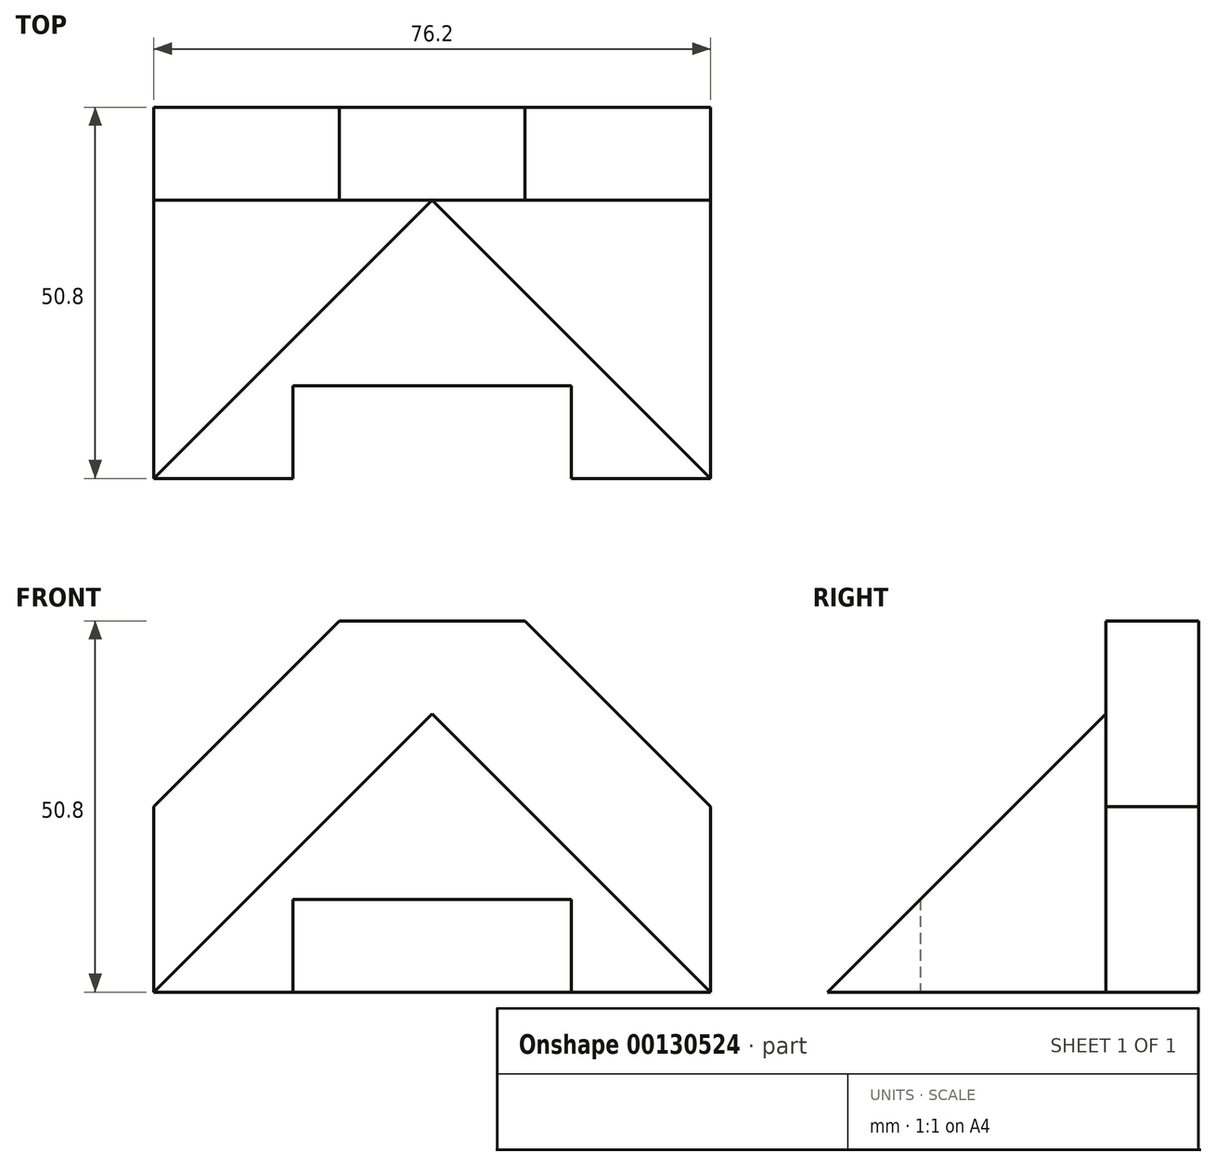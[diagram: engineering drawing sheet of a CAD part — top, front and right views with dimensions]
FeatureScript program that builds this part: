
annotation { "Feature Type Name" : "Feature", "Feature Type Description" : "" }
export const myFeature = defineFeature(function(context is Context, id is Id, definition is map)
    precondition{}
    {
        {
            var Q0;
            Q0=qCreatedBy(makeId("Front.planeOp"),FACE);
            var sketch = newSketch(context, id + "F0", { "sketchPlane" : qUnion([Q0])});
            skLineSegment(sketch, "E0", {"start": v(0, 0) * mm, "end": v(-76.2, 0) * mm});
            skLineSegment(sketch, "E1", {"start": v(-76.2, 0) * mm, "end": v(-76.2, 25.4) * mm});
            skLineSegment(sketch, "E2", {"start": v(-76.2, 25.4) * mm, "end": v(-50.8, 50.8) * mm});
            skLineSegment(sketch, "E3", {"start": v(-50.8, 50.8) * mm, "end": v(-25.4, 50.8) * mm});
            skLineSegment(sketch, "E4", {"start": v(-25.4, 50.8) * mm, "end": v(0, 25.4) * mm});
            skLineSegment(sketch, "E5", {"start": v(0, 25.4) * mm, "end": v(0, 0) * mm});
            skLineSegment(sketch, "E6", {"start": v(-76.2, 0) * mm, "end": v(-38.1, 38.1) * mm});
            skPoint(sketch, "E6.endSnap0", {"position": v(-38.1, 0) * mm});
            skLineSegment(sketch, "E7", {"start": v(-38.1, 38.1) * mm, "end": v(0, 0) * mm});
            skLineSegment(sketch, "E8", {"start": v(-57.15, 0) * mm, "end": v(-57.15, 12.7) * mm});
            skLineSegment(sketch, "E9", {"start": v(-57.15, 12.7) * mm, "end": v(-19.05, 12.7) * mm});
            skLineSegment(sketch, "E10", {"start": v(-19.05, 12.7) * mm, "end": v(-19.05, 0) * mm});
            skLineSegment(sketch, "E11", {"start": v(-19.05, 0) * mm, "end": v(-57.15, 0) * mm});
            skLineSegment(sketch, "E12", {"start": v(-38.1, 38.1) * mm, "end": v(-63.5, 38.1) * mm});
            skLineSegment(sketch, "E13", {"start": v(-63.5, 38.1) * mm, "end": v(-76.2, 25.4) * mm});
            skLineSegment(sketch, "E14", {"start": v(-38.1, 38.1) * mm, "end": v(-12.7, 38.1) * mm});
            skLineSegment(sketch, "E15", {"start": v(-12.7, 38.1) * mm, "end": v(0, 25.4) * mm});
            skLineSegment(sketch, "E16", {"start": v(0, 0) * mm, "end": v(-38.1, 38.1) * mm});
            skSolve(sketch);
        }
        {
            var Q0;
            Q0 = qSketchRegion(id + "F0", true);
            extrude(context, id + "F1", {"entities" : qUnion([Q0]), "endBound" : BoundingType.SYMMETRIC, "depth" : 50.8 * mm});
        }
        {
            var Q0;
            Q0=qCreatedBy(makeId("Right.planeOp"),FACE);
            var sketch = newSketch(context, id + "F2", { "sketchPlane" : qUnion([Q0])});
            skLineSegment(sketch, "E17", {"start": v(12.7, 50.8) * mm, "end": v(12.7, 38.1) * mm});
            skLineSegment(sketch, "E18", {"start": v(12.7, 38.1) * mm, "end": v(-25.4, 0) * mm});
            skLineSegment(sketch, "E19", {"start": v(-25.4, 0) * mm, "end": v(-25.4, 50.8) * mm});
            skLineSegment(sketch, "E20", {"start": v(-25.4, 50.8) * mm, "end": v(12.7, 50.8) * mm});
            skSolve(sketch);
        }
        {
            var Q0;
            Q0 = qSketchRegion(id + "F2", true);
            extrude(context, id + "F3", {"entities" : qUnion([Q0]), "operationType" : NewBodyOperationType.REMOVE, "endBound" : BoundingType.THROUGH_ALL, "oppositeDirection" : true, "depth" : 25.4 * mm});
        }
        {
            var Q0;
            Q0=qCreatedBy(makeId("Top.planeOp"),FACE);
            var sketch = newSketch(context, id + "F4", { "sketchPlane" : qUnion([Q0])});
            skLineSegment(sketch, "E21.bottom", {"start": v(-57.15, -25.4) * mm, "end": v(-19.05, -25.4) * mm});
            skLineSegment(sketch, "E21.top", {"start": v(-57.15, -12.7) * mm, "end": v(-19.05, -12.7) * mm});
            skLineSegment(sketch, "E21.left", {"start": v(-57.15, -25.4) * mm, "end": v(-57.15, -12.7) * mm});
            skLineSegment(sketch, "E21.right", {"start": v(-19.05, -25.4) * mm, "end": v(-19.05, -12.7) * mm});
            skSolve(sketch);
        }
        {
            var Q0;
            Q0 = qSketchRegion(id + "F4", true);
            extrude(context, id + "F5", {"entities" : qUnion([Q0]), "operationType" : NewBodyOperationType.REMOVE, "endBound" : BoundingType.THROUGH_ALL, "depth" : 25.4 * mm});
        }
        {
            var Q0;
            Q0=makeQuery(id+"F0.imprint","IMPRINT",FACE,{"disambiguationData":[TD([[makeQuery(id+"F0.imprint","IMPRINT",EDGE,{"derivedFrom":sQuery(id+"F0.wireOp",EDGE,"E1")}),-1.0]])]});
            var Q1;
            Q1=makeQuery(id+"F0.imprint","IMPRINT",FACE,{"disambiguationData":[TD([[makeQuery(id+"F0.imprint","IMPRINT",EDGE,{"derivedFrom":sQuery(id+"F0.wireOp",EDGE,"E5")}),-1.0]])]});
            extrude(context, id + "F6", {"entities" : qUnion([Q0, Q1]), "operationType" : NewBodyOperationType.REMOVE, "endBound" : BoundingType.SYMMETRIC, "oppositeDirection" : true, "depth" : 25.4 * mm});
        }
        {
            var Q0;
            Q0=makeQuery(id+"F0.imprint","IMPRINT",FACE,{"disambiguationData":[TD([[makeQuery(id+"F0.imprint","IMPRINT",EDGE,{"derivedFrom":sQuery(id+"F0.wireOp",EDGE,"E1")}),-1.0]])]});
            var Q1;
            Q1=makeQuery(id+"F0.imprint","IMPRINT",FACE,{"disambiguationData":[TD([[makeQuery(id+"F0.imprint","IMPRINT",EDGE,{"derivedFrom":sQuery(id+"F0.wireOp",EDGE,"E5")}),-1.0]])]});
            extrude(context, id + "F7", {"entities" : qUnion([Q0, Q1]), "operationType" : NewBodyOperationType.REMOVE, "depth" : 25.4 * mm});
        }
    });
